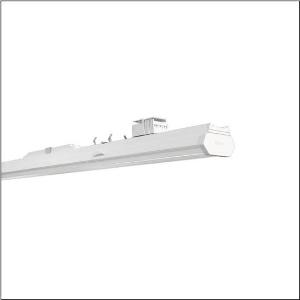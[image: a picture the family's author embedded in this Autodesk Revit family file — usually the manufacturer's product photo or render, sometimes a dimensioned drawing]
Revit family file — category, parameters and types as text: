
# Revit family: licross_r__11_protected_mo_51td11mn495g_5082
name_source: partatom
category: Lighting Fixtures
units: mm (PartAtom-declared; Revit-internal decimal feet)

## family parameters
Cut with Voids When Loaded = No
Host = Face
Light Source = No
Part Type = Normal
Room Calculation Point = No
Round Connector Dimension = Use Diameter
Shared = No

## types (1)
- --- (1 x LED, 9980 lm, 55.3 W, 4000K)
    Apparent Load = 55 VA
    CIE Flux Codes = 83 94 98 100 100
    Color Rendering = 80
    Color Temperature = 4000K
    Default Elevation = 1800 mm
    Description = Licross® 11 Protected MO, luminaire insert, of sheet steel, galvanised, coil coated, white, length: 1.500mm, width: 90mm, height: 101mm, LED rated luminous flux: 9.980lm, light colour: 840, control gear: ON/OFF Multilumen, with plug, 3-pole, with phase selection, mains connection: 220..240V, AC, 50/60Hz, rated input power: 55W, halogen-free wiring, primary light control with lens, of plastic, primary optical cover: cover, of PMMA, light emission: direct distribution, primary light characteristic: symmetric, protection rating (complete): IP54, insulation class (complete): insulation class I (protective earthing), certification: CE, ENEC, VDE, UKCA, protection symbol: D if used in an environment with non-conductive dust loads with corresponding accessories, impact resistance: IK06, permissible ambient temperature for indoor applications: -35..+40°C, corresponds to IFS (International Featured Standards) requirements for safety and quality in the food industry, reducing of maximum allowable ambient temperature of 5°C with ceiling mounting, LABS conformity tested according to VDMA 24364:2018-05, packaging unit: 1 piece
    Height = 92 mm
    Lamp = 1 x LED
    Lamp Light Flux = 9980 lm
    Lamp Power = 55.3 W
    Lamp count = 1
    Length = 1500 mm
    Luminous efficacy = 180 lm/W
    Manufacturer = Siteco
    ModVariant = No
    Model = 51TD11MN495G
    Mounting Place = Ceiling
    Mounting Type = Pendant
    Number of Poles = 1
    OnlyDefault = Yes
    Power Factor = 1
    Product Name = Licross® 11 Protected MO
    Product group = luminaire insert
    ProductGroupID = 901
    Protection Class = Protection class I
    Protection Degree = IP 54
    RLX_Detail_Level = 1
    RLX_Emergency_Light_Flux = 0 lm
    RLX_Emergency_Type = 0
    RLX_Emergency_Type_DB = No
    RlxData = <blob elided: 21793 chars, md5=2bf6183e>
    Socket = socket
    Standby Power = 0 W
    System Light Flux = 9980 lm
    System Power = 55 W
    Type Comments = factory setting: luminous flux: 100 % | (A | C | E) | 126 mA
    Type Image = l_1256145.jpg
    URL = http://relux.com
    VarID = @adj_055155
    Voltage = 0 V
    Weight = 0.00 kg
    Width = 88 mm

## geometry (parser evidence)
native form markers: Blend x4, Sweep x11
no freeform markers — native parametric forms only
